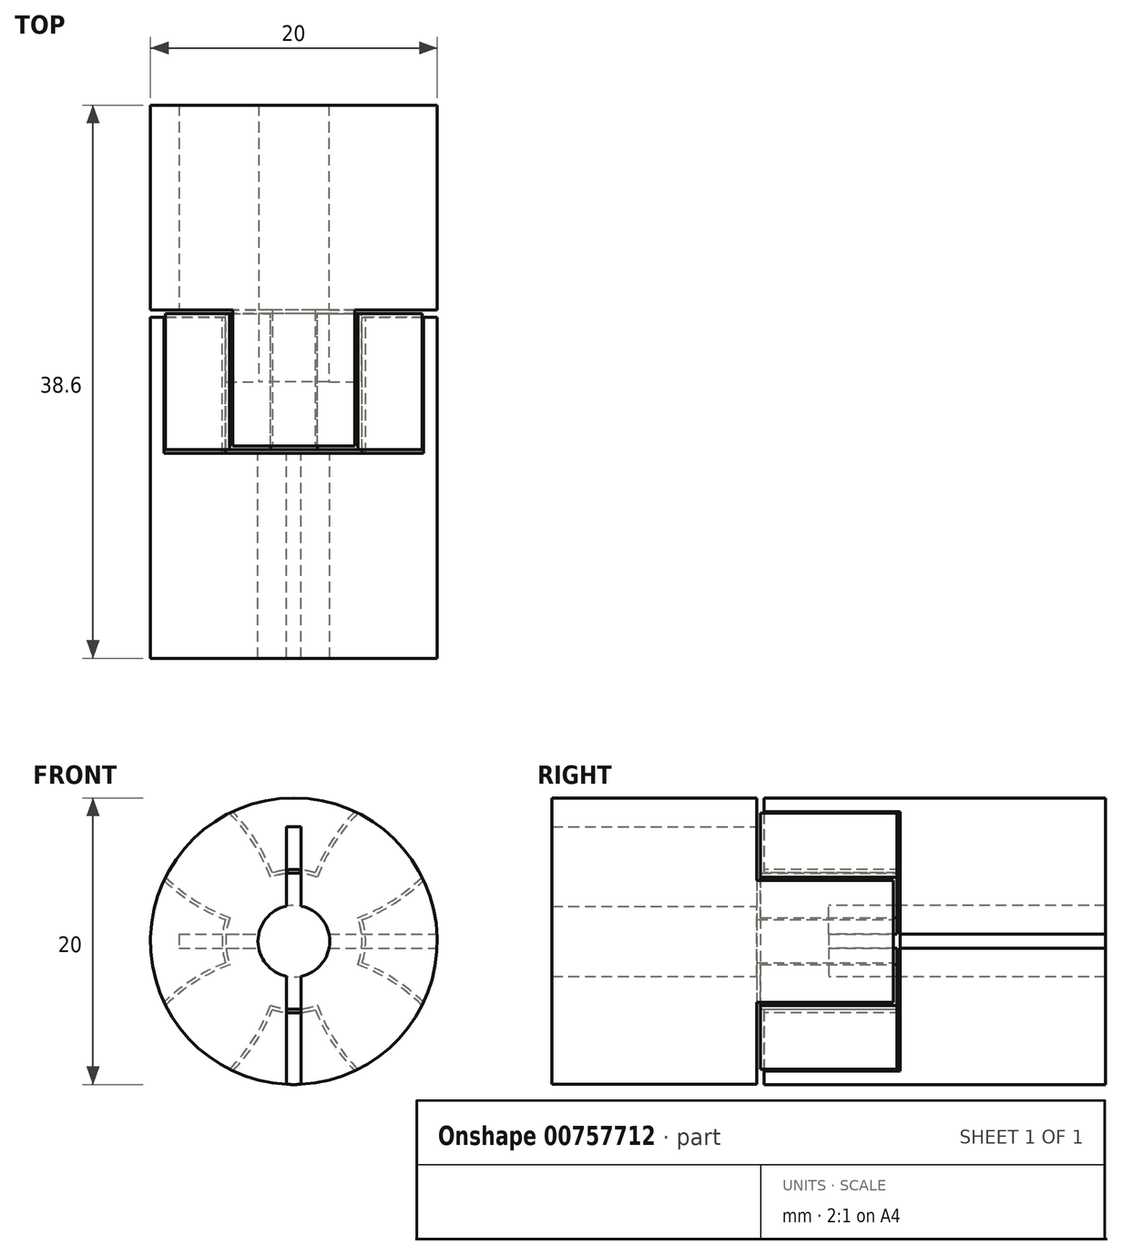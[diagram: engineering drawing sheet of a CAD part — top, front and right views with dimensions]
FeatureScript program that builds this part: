
annotation { "Feature Type Name" : "Feature", "Feature Type Description" : "" }
export const myFeature = defineFeature(function(context is Context, id is Id, definition is map)
    precondition{}
    {
        {
            var Q0;
            Q0=qCreatedBy(makeId("Front.planeOp"),FACE);
            var sketch = newSketch(context, id + "F0", { "sketchPlane" : qUnion([Q0])});
            skCircle(sketch, "E0", {"center": v(0, 0) * mm, "radius": 10 * mm});
            skSolve(sketch);
        }
        {
            var Q0;
            Q0=qCreatedBy(makeId("Front.planeOp"),FACE);
            var sketch = newSketch(context, id + "F1", { "sketchPlane" : qUnion([Q0])});
            skArc(sketch, "E1.0", {"start": v(-4.25, -9.05) * mm, "mid": v(0, -10) * mm, "end": v(4.25, -9.05) * mm});
            skArc(sketch, "E2", {"start": v(-1.5, -4.77) * mm, "mid": v(0, -5) * mm, "end": v(1.5, -4.77) * mm});
            skArc(sketch, "E3", {"start": v(-4.25, -9.05) * mm, "mid": v(-2.66, -7.05) * mm, "end": v(-1.5, -4.77) * mm});
            skArc(sketch, "E4", {"start": v(4.25, 9.05) * mm, "mid": v(2.66, 7.05) * mm, "end": v(1.5, 4.77) * mm});
            skLineSegment(sketch, "E5", {"start": v(0, -14.38) * mm, "end": v(0, 17.07) * mm, "construction": true});
            skPoint(sketch, "E6", {"position": v(-4.25, 9.05) * mm});
            skPoint(sketch, "E7", {"position": v(4.25, 9.05) * mm});
            skPoint(sketch, "E8", {"position": v(-1.5, 4.77) * mm});
            skPoint(sketch, "E9", {"position": v(1.5, 4.77) * mm});
            skArc(sketch, "E10.trimOffspring", {"start": v(4.25, 9.05) * mm, "mid": v(0, 10) * mm, "end": v(-4.25, 9.05) * mm});
            skArc(sketch, "E11.trimOffspring", {"start": v(1.5, 4.77) * mm, "mid": v(0, 5) * mm, "end": v(-1.5, 4.77) * mm});
            skArc(sketch, "E12.trimOffspring", {"start": v(1.5, -4.77) * mm, "mid": v(2.66, -7.05) * mm, "end": v(4.25, -9.05) * mm});
            skArc(sketch, "E13.trimOffspring", {"start": v(-1.5, 4.77) * mm, "mid": v(-2.66, 7.05) * mm, "end": v(-4.25, 9.05) * mm});
            skSolve(sketch);
        }
        {
            var Q0;
            Q0=qCreatedBy(makeId("Front.planeOp"),FACE);
            var sketch = newSketch(context, id + "F2", { "sketchPlane" : qUnion([Q0])});
            skArc(sketch, "E14", {"start": v(-1.64, 4.46) * mm, "mid": v(-2.82, 6.85) * mm, "end": v(-4.48, 8.94) * mm});
            skLineSegment(sketch, "E15", {"start": v(0, 0) * mm, "end": v(-15.65, 15.65) * mm, "construction": true});
            skArc(sketch, "E16.MirrorC", {"start": v(-4.46, 1.64) * mm, "mid": v(-6.85, 2.82) * mm, "end": v(-8.94, 4.48) * mm});
            skArc(sketch, "E17", {"start": v(-4.46, 1.64) * mm, "mid": v(3.36, -3.36) * mm, "end": v(-1.64, 4.46) * mm});
            skArc(sketch, "E18", {"start": v(-4.48, 8.94) * mm, "mid": v(-7.07, 7.07) * mm, "end": v(-8.94, 4.48) * mm});
            skSolve(sketch);
        }
        {
            var Q0;
            Q0=makeQuery(id+"F2.imprint","IMPRINT",FACE,{"disambiguationData":[TD([[makeQuery(id+"F2.imprint","IMPRINT",EDGE,{"derivedFrom":sQuery(id+"F2.wireOp",EDGE,"E14")}),1.0]])]});
            extrude(context, id + "F3", {"entities" : qUnion([Q0]), "endBound" : BoundingType.SYMMETRIC, "depth" : 9.5 * mm, "offsetDistance" : 25 * mm});
        }
        {
            var Q0;
            Q0=makeQuery(id+"F3.opExtrude","SWEPT_BODY",BODY,{"disambiguationData":[OSD([sQuery(id+"F2.wireOp",EDGE,"E14"),sQuery(id+"F2.wireOp",EDGE,"E16.MirrorC"),sQuery(id+"F2.wireOp",EDGE,"E17"),sQuery(id+"F2.wireOp",EDGE,"E18")])]});
            var Q1;
            Q1=makeQuery(id+"F3.opExtrude","SWEPT_FACE",FACE,{"disambiguationData":[OSD([sQuery(id+"F2.wireOp",EDGE,"E17")])]});
            circularPattern(context, id + "F4", {"operationType" : NewBodyOperationType.ADD, "entities" : qUnion([Q0]), "axis" : qUnion([Q1]), "angle" : 360 * degree, "instanceCount" : 4, "equalSpace" : true});
        }
        {
            var Q0;
            Q0=makeQuery(id+"F0.imprint","IMPRINT",FACE,{"disambiguationData":[TD([[makeQuery(id+"F0.imprint","IMPRINT",EDGE,{"derivedFrom":sQuery(id+"F0.wireOp",EDGE,"E0")}),1.0]])]});
            extrude(context, id + "F5", {"entities" : qUnion([Q0]), "oppositeDirection" : true, "depth" : 19.3 * mm, "offsetDistance" : 25 * mm, "hasSecondDirection" : true, "secondDirectionOppositeDirection" : true, "secondDirectionDepth" : 5 * mm});
        }
        {
            var Q0;
            Q0=qCreatedBy(makeId("Front.planeOp"),FACE);
            var sketch = newSketch(context, id + "F6", { "sketchPlane" : qUnion([Q0])});
            skLineSegment(sketch, "E19.bottom", {"start": v(-8, 0.5) * mm, "end": v(10, 0.5) * mm});
            skLineSegment(sketch, "E19.top", {"start": v(-8, -0.5) * mm, "end": v(10, -0.5) * mm});
            skLineSegment(sketch, "E19.left", {"start": v(-8, 0.5) * mm, "end": v(-8, -0.5) * mm});
            skLineSegment(sketch, "E19.right", {"start": v(10, 0.5) * mm, "end": v(10, -0.5) * mm});
            skPoint(sketch, "E19.middle", {"position": v(1, 0) * mm});
            skSolve(sketch);
        }
        {
            var Q0;
            Q0 = qSketchRegion(id + "F6", true);
            extrude(context, id + "F7", {"entities" : qUnion([Q0]), "operationType" : NewBodyOperationType.REMOVE, "oppositeDirection" : true, "depth" : 25 * mm, "offsetDistance" : 25 * mm});
        }
        {
            var Q0;
            Q0=makeQuery(id+"F1.imprint","IMPRINT",FACE,{"disambiguationData":[TD([[makeQuery(id+"F1.imprint","IMPRINT",EDGE,{"derivedFrom":sQuery(id+"F1.wireOp",EDGE,"E4")}),-1.0]])]});
            var Q1;
            Q1=makeQuery(id+"F1.imprint","IMPRINT",FACE,{"disambiguationData":[TD([[makeQuery(id+"F1.imprint","IMPRINT",EDGE,{"derivedFrom":sQuery(id+"F1.wireOp",EDGE,"E1.0")}),1.0]])]});
            extrude(context, id + "F8", {"entities" : qUnion([Q0, Q1]), "operationType" : NewBodyOperationType.ADD, "endBound" : BoundingType.UP_TO_NEXT, "oppositeDirection" : true, "depth" : 25 * mm, "offsetDistance" : 25 * mm, "hasSecondDirection" : true, "secondDirectionOppositeDirection" : false, "secondDirectionDepth" : 4.5 * mm});
        }
        {
            var Q0;
            Q0=qCreatedBy(makeId("Front.planeOp"),FACE);
            var sketch = newSketch(context, id + "F9", { "sketchPlane" : qUnion([Q0])});
            skCircle(sketch, "E20", {"center": v(0, 0) * mm, "radius": 2.5 * mm});
            skSolve(sketch);
        }
        {
            var Q0;
            Q0 = qSketchRegion(id + "F9", true);
            extrude(context, id + "F10", {"entities" : qUnion([Q0]), "operationType" : NewBodyOperationType.REMOVE, "endBound" : BoundingType.THROUGH_ALL, "oppositeDirection" : true, "depth" : 25 * mm, "offsetDistance" : 25 * mm});
        }
        {
            var Q0;
            Q0=makeQuery(id+"F5.opExtrude","SWEPT_BODY",BODY,{"disambiguationData":[OSD([sQuery(id+"F0.wireOp",EDGE,"E0")])]});
            var Q1;
            Q1=qCreatedBy(makeId("Front.planeOp"),FACE);
            mirror(context, id + "F11", {"entities" : qUnion([Q0]), "mirrorPlane" : qUnion([Q1])});
        }
        {
            var Q0;
            Q0=makeQuery(id+"F11.opPattern","COPY",BODY,{"derivedFrom":makeQuery(id+"F5.opExtrude","SWEPT_BODY",BODY,{"disambiguationData":[OSD([sQuery(id+"F0.wireOp",EDGE,"E0")])]}),"instanceName":"1"});
            var Q1;
            Q1=makeQuery(id+"F11.opPattern","COPY",FACE,{"derivedFrom":makeQuery(id+"F8.boolean.opBoolean","MERGE",FACE,{"derivedFrom":[makeQuery(id+"F5.opExtrude","SWEPT_FACE",FACE,{"disambiguationData":[OSD([sQuery(id+"F0.wireOp",EDGE,"E0")])]}),makeQuery(id+"F8.opExtrude","SWEPT_FACE",FACE,{"disambiguationData":[OSD([sQuery(id+"F1.wireOp",EDGE,"E1.0")])]}),makeQuery(id+"F8.opExtrude","SWEPT_FACE",FACE,{"disambiguationData":[OSD([sQuery(id+"F1.wireOp",EDGE,"E10.trimOffspring")])]})]}),"instanceName":"1"});
            transform(context, id + "F12", {"entities" : qUnion([Q0]), "transformType" : TransformType.ROTATION, "transformAxis" : qUnion([Q1]), "angle" : 90 * degree, "makeCopy" : false});
        }
    });
